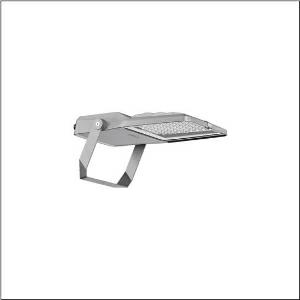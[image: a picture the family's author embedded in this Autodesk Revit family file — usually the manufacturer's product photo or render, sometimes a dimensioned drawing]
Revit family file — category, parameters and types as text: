
# Revit family: floodlight_fl_21_iq_mini___rs12_5xa7771d2b1a_498a
name_source: partatom
category: Lighting Fixtures
units: mm (PartAtom-declared; Revit-internal decimal feet)

## family parameters
Cut with Voids When Loaded = No
Host = Face
Light Source = No
Part Type = Normal
Room Calculation Point = No
Round Connector Dimension = Use Diameter
Shared = No

## types (1)
- --- (1 x LED, 18020 lm, 143 W, 3000K)
    Apparent Load = 143 VA
    CIE Flux Codes = 79 92 99 100 100
    Color Rendering = 70
    Color Temperature = 3000K
    Default Elevation = 1800 mm
    Description = Floodlight FL 21 iQ mini, floodlight, primary light control with lens, of PMMA, primary optical cover: protective disc, of toughened safety glass, transparent, light distribution: RS12, light emission: direct distribution, installation type: surface-mounted, LED, High Power LED, rated luminous flux: 18.020lm, luminous efficacy: 126lm/W, light colour: 730, colour temperature: 3000K, control gear: iQ Comfort/DALI, control: Auto-Match, Temp-Guard, Lumen-Switch, Night-Set, Smart-Wire, Light-Fading, Desk-Remote (wireless, voltage-free reading and setting of iQ features in the workshop via application-optimized NFC function/RFID function), optimised constant luminous flux control (CLO 2.0), with terminal, 6-pole, mains connection: 220..240V, AC, 50/60Hz, start of lifetime: 143W, end of service life: 152W, reduction: 61W, luminaire housing, of diecast aluminium, powder-coated, Siteco® metallic grey (DB 702S), corrosivity category C5 mid according to DIN EN ISO 12944, suitable for swimming pools, chlorine-resistant, sealing non-destructively replaceable, mounting bracket, of steel, galvanised, powder-coated, Siteco® metallic grey (DB 702S), protection rating (complete): IP66, insulation class (complete): insulation class II (safety insulation), certification: CE, ENEC, VDE, protection symbol: D, impact resistance: IK08, permissible operating ambient temperature: -40..+40°C, permissible operating ambient temperature for outdoor applications: -40..+50°C, standard: DIN EN 12944, LABS conformity tested according to VDMA 24364:2018-05, packaging unit: 1 piece

Light Distribution: RS12
    Height = 70 mm
    Lamp = 1 x LED
    Lamp Light Flux = 18020 lm
    Lamp Power = 143 W
    Lamp count = 1
    Length = 485 mm
    Luminous efficacy = 126 lm/W
    Manufacturer = Siteco
    ModVariant = No
    Model = 5XA7771D2B1A
    Number of Poles = 1
    OnlyDefault = Yes
    Power Factor = 1
    Product Name = Floodlight FL 21 iQ mini | RS12
    Product group = floodlight | pylon annexe
    ProductGroupID = 6200
    Protection Class = Protection class II
    Protection Degree = IP 66
    RLX_Detail_Level = 1
    RLX_Emergency_Light_Flux = 0 lm
    RLX_Emergency_Type = 0
    RLX_Emergency_Type_DB = No
    RlxData = <blob elided: 91229 chars, md5=2714f79a>
    Socket = socket
    Standby Power = 0 W
    System Light Flux = 18020 lm
    System Power = 143 W
    Type Comments = factory setting: luminous flux: 100 % | dim-lin: 254 | 730 mA
    Type Image = l_1006845.jpg
    URL = http://relux.com
    VarID = @adj_167490
    Voltage = 0 V
    Weight = 0.00 kg
    Width = 337 mm

## geometry (parser evidence)
native form markers: Blend x4, Sweep x13
no freeform markers — native parametric forms only
